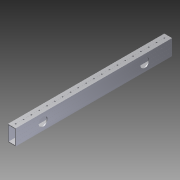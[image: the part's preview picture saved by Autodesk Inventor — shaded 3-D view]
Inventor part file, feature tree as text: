
AUTODESK INVENTOR PART (.ipt)
format: ipt  version: 2014 (Build 180170000, 170)  size: 747,008 bytes
history: native  units: in
note: dims shown in document units (in); Inventor stores cm internally (conversion verified against a paired STEP export)
features: extrude x3, sketch x3, other x2, imported_body x1
ambient origin geometry x8: Origin, YZ Plane, XZ Plane, XY Plane, X Axis, Y Axis, Z Axis, Center Point
bodies: Body1 (feature_tree)
feature tree (9):
  other  "Cut-Extrude2"
  other  "2x1 Tube1"
  extrude  "Extrusion1"  Depth=1.125in
  extrude  "Extrusion2"  Depth=0.5in TaperAngle=0.0deg
  extrude  "Extrusion3"  Depth=3.5in
  imported_body  "Base1"
  sketch  "Sketch1"  dims[d0=39.0in d1=0.0in d2=1.125in]
  sketch  "Sketch2"  dims[d3=3.5in d4=0.5in d5=0.0in]
  sketch  "Sketch4"  dims[d6=1.125in d7=3.5in d8=0.5in d9=0.0in]
